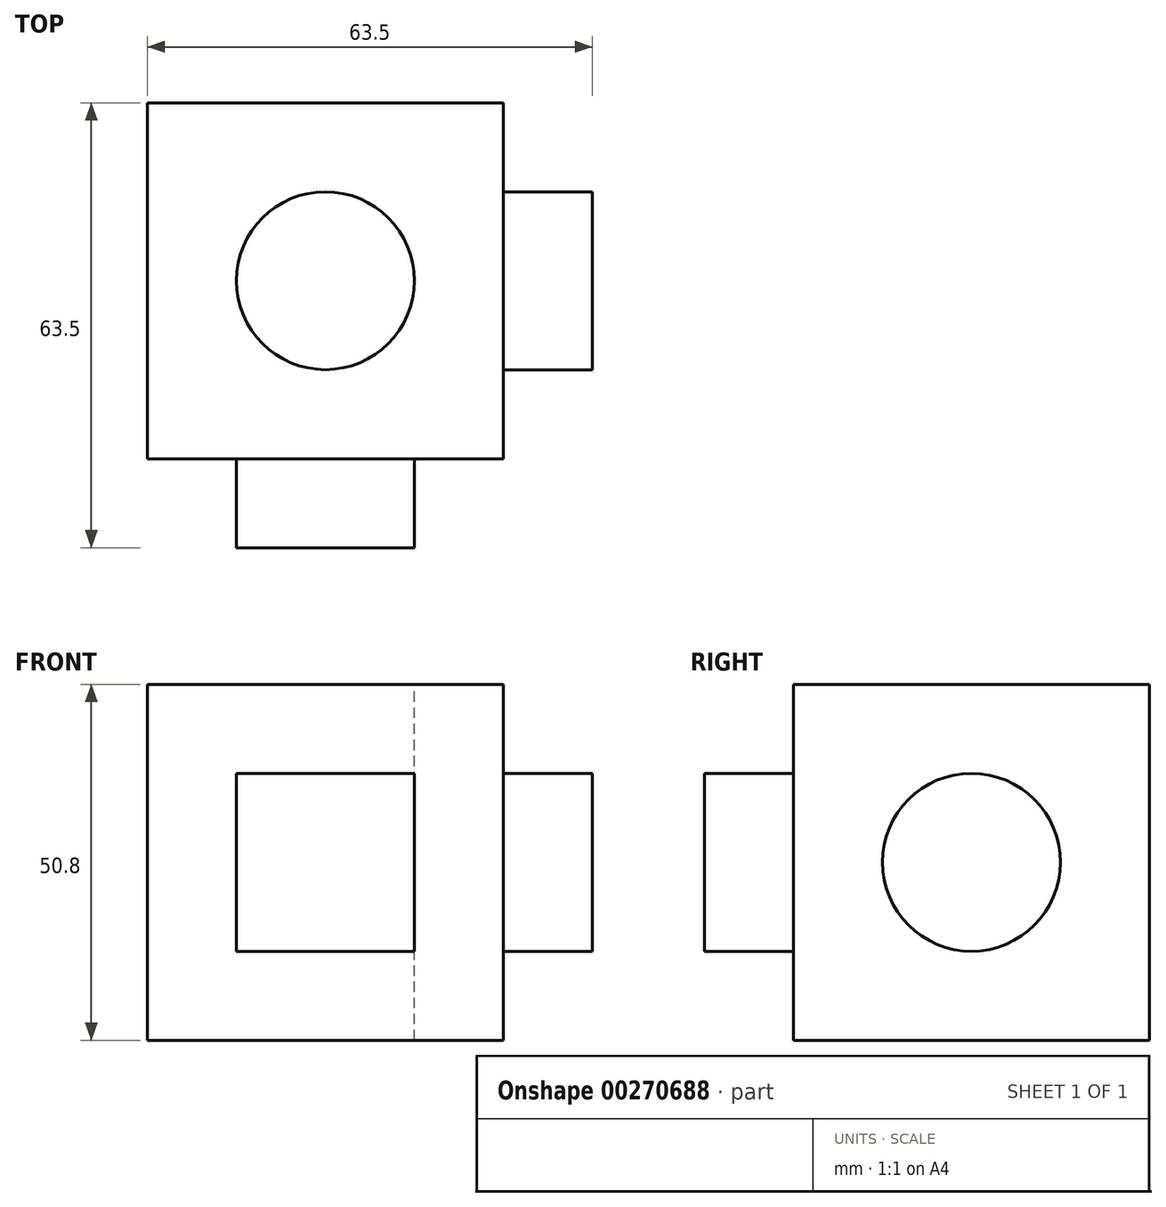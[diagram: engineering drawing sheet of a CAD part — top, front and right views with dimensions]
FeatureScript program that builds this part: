
annotation { "Feature Type Name" : "Feature", "Feature Type Description" : "" }
export const myFeature = defineFeature(function(context is Context, id is Id, definition is map)
    precondition{}
    {
        {
            var Q0;
            Q0=qCreatedBy(makeId("Front.planeOp"),FACE);
            var sketch = newSketch(context, id + "F0", { "sketchPlane" : qUnion([Q0])});
            skLineSegment(sketch, "E0.bottom", {"start": v(0, 0) * mm, "end": v(-50.8, 0) * mm});
            skLineSegment(sketch, "E0.top", {"start": v(0, 50.8) * mm, "end": v(-50.8, 50.8) * mm});
            skLineSegment(sketch, "E0.left", {"start": v(0, 0) * mm, "end": v(0, 50.8) * mm});
            skLineSegment(sketch, "E0.right", {"start": v(-50.8, 0) * mm, "end": v(-50.8, 50.8) * mm});
            skSolve(sketch);
        }
        {
            var Q0;
            Q0=makeQuery(id+"F0.imprint","IMPRINT",FACE,{"disambiguationData":[TD([[makeQuery(id+"F0.imprint","IMPRINT",EDGE,{"derivedFrom":sQuery(id+"F0.wireOp",EDGE,"E0.bottom")}),-1.0]])]});
            extrude(context, id + "F1", {"entities" : qUnion([Q0]), "depth" : 50.8 * mm});
        }
        {
            var Q0;
            Q0=makeQuery(id+"F1.opExtrude","CAP_FACE",FACE,{"disambiguationData":[OSD([sQuery(id+"F0.wireOp",EDGE,"E0.bottom"),sQuery(id+"F0.wireOp",EDGE,"E0.top"),sQuery(id+"F0.wireOp",EDGE,"E0.left"),sQuery(id+"F0.wireOp",EDGE,"E0.right")])],"isStart":false});
            var sketch = newSketch(context, id + "F2", { "sketchPlane" : qUnion([Q0])});
            skLineSegment(sketch, "E1.bottom", {"start": v(-38.1, 38.1) * mm, "end": v(-12.7, 38.1) * mm});
            skLineSegment(sketch, "E1.top", {"start": v(-38.1, 12.7) * mm, "end": v(-12.7, 12.7) * mm});
            skLineSegment(sketch, "E1.left", {"start": v(-38.1, 38.1) * mm, "end": v(-38.1, 12.7) * mm});
            skLineSegment(sketch, "E1.right", {"start": v(-12.7, 38.1) * mm, "end": v(-12.7, 12.7) * mm});
            skSolve(sketch);
        }
        {
            var Q0;
            Q0=makeQuery(id+"F2.imprint","IMPRINT",FACE,{"disambiguationData":[TD([[makeQuery(id+"F2.imprint","IMPRINT",EDGE,{"derivedFrom":sQuery(id+"F2.wireOp",EDGE,"E1.bottom")}),-1.0]])]});
            extrude(context, id + "F3", {"entities" : qUnion([Q0]), "operationType" : NewBodyOperationType.ADD, "depth" : 12.7 * mm});
        }
        {
            var Q0;
            Q0=makeQuery(id+"F1.opExtrude","SWEPT_FACE",FACE,{"disambiguationData":[OSD([sQuery(id+"F0.wireOp",EDGE,"E0.left")])]});
            var sketch = newSketch(context, id + "F4", { "sketchPlane" : qUnion([Q0])});
            skCircle(sketch, "E2", {"center": v(-25.4, 25.4) * mm, "radius": 12.7 * mm});
            skSolve(sketch);
        }
        {
            var Q0;
            Q0=makeQuery(id+"F4.imprint","IMPRINT",FACE,{"disambiguationData":[TD([[makeQuery(id+"F4.imprint","IMPRINT",EDGE,{"derivedFrom":sQuery(id+"F4.wireOp",EDGE,"E2")}),1.0]])]});
            extrude(context, id + "F5", {"entities" : qUnion([Q0]), "operationType" : NewBodyOperationType.ADD, "depth" : 12.7 * mm});
        }
        {
            var Q0;
            Q0=makeQuery(id+"F1.opExtrude","SWEPT_FACE",FACE,{"disambiguationData":[OSD([sQuery(id+"F0.wireOp",EDGE,"E0.top")])]});
            var sketch = newSketch(context, id + "F6", { "sketchPlane" : qUnion([Q0])});
            skCircle(sketch, "E3", {"center": v(-25.4, -25.4) * mm, "radius": 12.7 * mm});
            skSolve(sketch);
        }
        {
            var Q0;
            Q0=makeQuery(id+"F6.imprint","IMPRINT",FACE,{"disambiguationData":[TD([[makeQuery(id+"F6.imprint","IMPRINT",EDGE,{"derivedFrom":sQuery(id+"F6.wireOp",EDGE,"E3")}),1.0]])]});
            extrude(context, id + "F7", {"entities" : qUnion([Q0]), "operationType" : NewBodyOperationType.REMOVE, "oppositeDirection" : true, "depth" : 50.8 * mm});
        }
    });
